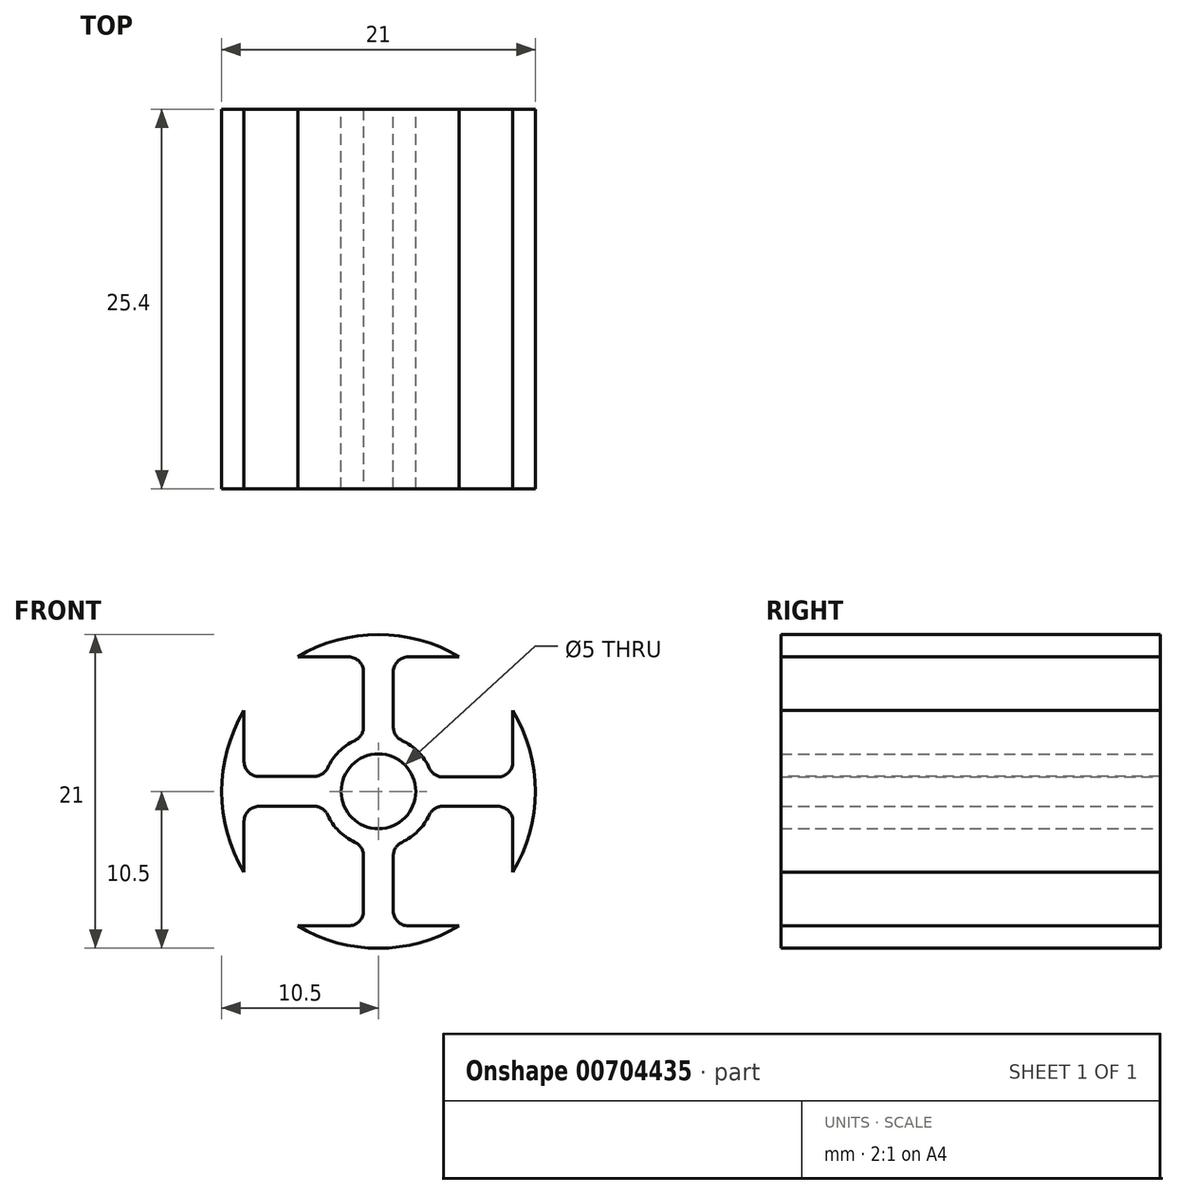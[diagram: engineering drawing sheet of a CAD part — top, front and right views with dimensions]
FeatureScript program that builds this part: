
annotation { "Feature Type Name" : "Feature", "Feature Type Description" : "" }
export const myFeature = defineFeature(function(context is Context, id is Id, definition is map)
    precondition{}
    {
        {
            var Q0;
            Q0=qCreatedBy(makeId("Front.planeOp"),FACE);
            var sketch = newSketch(context, id + "F0", { "sketchPlane" : qUnion([Q0])});
            skArc(sketch, "E0", {"start": v(-9, 5.4) * mm, "mid": v(-10.5, 0) * mm, "end": v(-9, -5.4) * mm});
            skLineSegment(sketch, "E1.bottom", {"start": v(5.4, 9) * mm, "end": v(-5.4, 9) * mm});
            skLineSegment(sketch, "E1.top", {"start": v(5.4, -9) * mm, "end": v(-5.4, -9) * mm});
            skLineSegment(sketch, "E1.left", {"start": v(9, 5.4) * mm, "end": v(9, -5.4) * mm});
            skLineSegment(sketch, "E1.right", {"start": v(-9, 5.4) * mm, "end": v(-9, -5.4) * mm});
            skLineSegment(sketch, "E2.bottom", {"start": v(-3.75, 0) * mm, "end": v(-9, 0) * mm});
            skLineSegment(sketch, "E2.right", {"start": v(-9, 0) * mm, "end": v(-9, 1) * mm});
            skLineSegment(sketch, "E3.right", {"start": v(-9, 0) * mm, "end": v(-9, -1) * mm});
            skLineSegment(sketch, "E4.bottom", {"start": v(3.75, 0) * mm, "end": v(9, 0) * mm});
            skLineSegment(sketch, "E4.right", {"start": v(9, 0) * mm, "end": v(9, 0.96) * mm});
            skLineSegment(sketch, "E5.right", {"start": v(9, 0) * mm, "end": v(9, -1) * mm});
            skLineSegment(sketch, "E6.top", {"start": v(0, 9) * mm, "end": v(1, 9) * mm});
            skLineSegment(sketch, "E7.top", {"start": v(0, 9) * mm, "end": v(-1, 9) * mm});
            skLineSegment(sketch, "E8.top", {"start": v(0, -9) * mm, "end": v(1, -9) * mm});
            skLineSegment(sketch, "E9.top", {"start": v(0, -9) * mm, "end": v(-1, -9) * mm});
            skLineSegment(sketch, "E9.right", {"start": v(-1, -3.61) * mm, "end": v(-1, -9) * mm});
            skPoint(sketch, "E10", {"position": v(-5.4, 9) * mm});
            skPoint(sketch, "E11", {"position": v(-9, 5.4) * mm});
            skPoint(sketch, "E12", {"position": v(-9, 9) * mm});
            skArc(sketch, "E13.trimOffspring", {"start": v(-5.4, -9) * mm, "mid": v(0, -10.5) * mm, "end": v(5.4, -9) * mm});
            skPoint(sketch, "E14.orphan", {"position": v(-9, -9) * mm});
            skPoint(sketch, "E15.orphan", {"position": v(9, -9) * mm});
            skArc(sketch, "E16.trimOffspring", {"start": v(9, -5.4) * mm, "mid": v(10.5, 0) * mm, "end": v(9, 5.4) * mm});
            skArc(sketch, "E17.trimOffspring", {"start": v(5.4, 9) * mm, "mid": v(0, 10.5) * mm, "end": v(-5.4, 9) * mm});
            skPoint(sketch, "E18.orphan", {"position": v(9, 9) * mm});
            skLineSegment(sketch, "E19.trimOffspring", {"start": v(3.62, 0.96) * mm, "end": v(9, 0.96) * mm});
            skLineSegment(sketch, "E20.trimOffspring", {"start": v(1, 3.61) * mm, "end": v(1, 9) * mm});
            skLineSegment(sketch, "E21.trimOffspring", {"start": v(0, 3.75) * mm, "end": v(0, 9) * mm});
            skLineSegment(sketch, "E22.trimOffspring", {"start": v(-1, 3.61) * mm, "end": v(-1, 9) * mm});
            skLineSegment(sketch, "E23.trimOffspring", {"start": v(-3.61, 1) * mm, "end": v(-9, 1) * mm});
            skLineSegment(sketch, "E24.trimOffspring", {"start": v(-3.61, -1) * mm, "end": v(-9, -1) * mm});
            skLineSegment(sketch, "E25.trimOffspring", {"start": v(3.61, -1) * mm, "end": v(9, -1) * mm});
            skCircle(sketch, "E26", {"center": v(0, 0) * mm, "radius": 3.75 * mm});
            skLineSegment(sketch, "E27.trimOffspring", {"start": v(1, -3.61) * mm, "end": v(1, -9) * mm});
            skLineSegment(sketch, "E28.trimOffspring", {"start": v(0, -3.75) * mm, "end": v(0, -9) * mm});
            skCircle(sketch, "E29", {"center": v(0, 0) * mm, "radius": 2.5 * mm});
            skPoint(sketch, "E30", {"position": v(0, 2.5) * mm});
            skPoint(sketch, "E31", {"position": v(2.5, 0) * mm});
            skPoint(sketch, "E32", {"position": v(0, -2.5) * mm});
            skPoint(sketch, "E33", {"position": v(-2.5, 0) * mm});
            skLineSegment(sketch, "E34", {"start": v(0, 0) * mm, "end": v(-2.5, 0) * mm});
            skLineSegment(sketch, "E35", {"start": v(0, 0) * mm, "end": v(0, 2.5) * mm});
            skLineSegment(sketch, "E36", {"start": v(0, 0) * mm, "end": v(2.5, 0) * mm});
            skLineSegment(sketch, "E37", {"start": v(0, 0) * mm, "end": v(0, -2.5) * mm});
            skSolve(sketch);
        }
        {
            var Q0;
            Q0 = qSketchRegion(id + "F0", true);
            extrude(context, id + "F1", {"entities" : qUnion([Q0]), "depth" : 25.4 * mm, "offsetDistance" : 25.4 * mm});
        }
        {
            var Q0;
            Q0=makeQuery(id+"F1.opExtrude","SWEPT_EDGE",EDGE,{"disambiguationData":[OSD([sQuery(id+"F0.wireOp",EDGE,"E24.trimOffspring"),sQuery(id+"F0.wireOp",EDGE,"E26")])]});
            var Q1;
            Q1=makeQuery(id+"F1.opExtrude","SWEPT_EDGE",EDGE,{"disambiguationData":[OSD([sQuery(id+"F0.wireOp",EDGE,"E1.right"),sQuery(id+"F0.wireOp",EDGE,"E3.right"),sQuery(id+"F0.wireOp",EDGE,"E24.trimOffspring")])]});
            var Q2;
            Q2=makeQuery(id+"F1.opExtrude","SWEPT_EDGE",EDGE,{"disambiguationData":[OSD([sQuery(id+"F0.wireOp",EDGE,"E1.right"),sQuery(id+"F0.wireOp",EDGE,"E2.right"),sQuery(id+"F0.wireOp",EDGE,"E23.trimOffspring")])]});
            var Q3;
            Q3=makeQuery(id+"F1.opExtrude","SWEPT_EDGE",EDGE,{"disambiguationData":[OSD([sQuery(id+"F0.wireOp",EDGE,"E19.trimOffspring"),sQuery(id+"F0.wireOp",EDGE,"E26")])]});
            var Q4;
            Q4=makeQuery(id+"F1.opExtrude","SWEPT_EDGE",EDGE,{"disambiguationData":[OSD([sQuery(id+"F0.wireOp",EDGE,"E20.trimOffspring"),sQuery(id+"F0.wireOp",EDGE,"E26")])]});
            var Q5;
            Q5=makeQuery(id+"F1.opExtrude","SWEPT_EDGE",EDGE,{"disambiguationData":[OSD([sQuery(id+"F0.wireOp",EDGE,"E26"),sQuery(id+"F0.wireOp",EDGE,"E27.trimOffspring")])]});
            var Q6;
            Q6=makeQuery(id+"F1.opExtrude","SWEPT_EDGE",EDGE,{"disambiguationData":[OSD([sQuery(id+"F0.wireOp",EDGE,"E25.trimOffspring"),sQuery(id+"F0.wireOp",EDGE,"E26")])]});
            var Q7;
            Q7=makeQuery(id+"F1.opExtrude","SWEPT_EDGE",EDGE,{"disambiguationData":[OSD([sQuery(id+"F0.wireOp",EDGE,"E1.top"),sQuery(id+"F0.wireOp",EDGE,"E8.top"),sQuery(id+"F0.wireOp",EDGE,"E27.trimOffspring")])]});
            var Q8;
            Q8=makeQuery(id+"F1.opExtrude","SWEPT_EDGE",EDGE,{"disambiguationData":[OSD([sQuery(id+"F0.wireOp",EDGE,"E1.top"),sQuery(id+"F0.wireOp",EDGE,"E9.top"),sQuery(id+"F0.wireOp",EDGE,"E9.right")])]});
            var Q9;
            Q9=makeQuery(id+"F1.opExtrude","SWEPT_EDGE",EDGE,{"disambiguationData":[OSD([sQuery(id+"F0.wireOp",EDGE,"E1.bottom"),sQuery(id+"F0.wireOp",EDGE,"E7.top"),sQuery(id+"F0.wireOp",EDGE,"E22.trimOffspring")])]});
            var Q10;
            Q10=makeQuery(id+"F1.opExtrude","SWEPT_EDGE",EDGE,{"disambiguationData":[OSD([sQuery(id+"F0.wireOp",EDGE,"E1.bottom"),sQuery(id+"F0.wireOp",EDGE,"E6.top"),sQuery(id+"F0.wireOp",EDGE,"E20.trimOffspring")])]});
            var Q11;
            Q11=makeQuery(id+"F1.opExtrude","SWEPT_EDGE",EDGE,{"disambiguationData":[OSD([sQuery(id+"F0.wireOp",EDGE,"E1.left"),sQuery(id+"F0.wireOp",EDGE,"E5.right"),sQuery(id+"F0.wireOp",EDGE,"E25.trimOffspring")])]});
            var Q12;
            Q12=makeQuery(id+"F1.opExtrude","SWEPT_EDGE",EDGE,{"disambiguationData":[OSD([sQuery(id+"F0.wireOp",EDGE,"E1.left"),sQuery(id+"F0.wireOp",EDGE,"E4.right"),sQuery(id+"F0.wireOp",EDGE,"E19.trimOffspring")])]});
            var Q13;
            Q13=makeQuery(id+"F1.opExtrude","SWEPT_EDGE",EDGE,{"disambiguationData":[OSD([sQuery(id+"F0.wireOp",EDGE,"E22.trimOffspring"),sQuery(id+"F0.wireOp",EDGE,"E26")])]});
            var Q14;
            Q14=makeQuery(id+"F1.opExtrude","SWEPT_EDGE",EDGE,{"disambiguationData":[OSD([sQuery(id+"F0.wireOp",EDGE,"E23.trimOffspring"),sQuery(id+"F0.wireOp",EDGE,"E26")])]});
            var Q15;
            Q15=makeQuery(id+"F1.opExtrude","SWEPT_EDGE",EDGE,{"disambiguationData":[OSD([sQuery(id+"F0.wireOp",EDGE,"E9.right"),sQuery(id+"F0.wireOp",EDGE,"E26")])]});
            fillet(context, id + "F2", {"entities" : qUnion([Q0, Q1, Q2, Q3, Q4, Q5, Q6, Q7, Q8, Q9, Q10, Q11, Q12, Q13, Q14, Q15]), "radius" : 1 * mm, "tangentPropagation" : true, "allowEdgeOverflow" : false});
        }
    });
